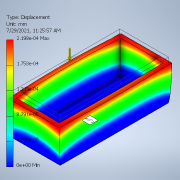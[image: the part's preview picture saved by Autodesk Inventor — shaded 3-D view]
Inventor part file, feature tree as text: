
AUTODESK INVENTOR PART (.ipt)
format: ipt  version: 2021 (Build 250183000, 183)  size: 151,552 bytes
history: native  units: mm
features: extrude x1, shell x1, sketch x1
ambient origin geometry x8: Origin, YZ Plane, XZ Plane, XY Plane, X Axis, Y Axis, Z Axis, Center Point
bodies: Solid1 (feature_tree)
feature tree (3):
  extrude  "Extrusion1"  Depth=1.0mm
  shell  "Shell1"  [1 undecoded]
  sketch  "Sketch1"  dims[d0=10.0mm d1=0.0mm d2=1.0mm]
note: 1 required parameter value undecoded (feature->parameter linkage not recoverable at this tier; creation-order binding heuristic only, values carry confidence <= 0.55)
